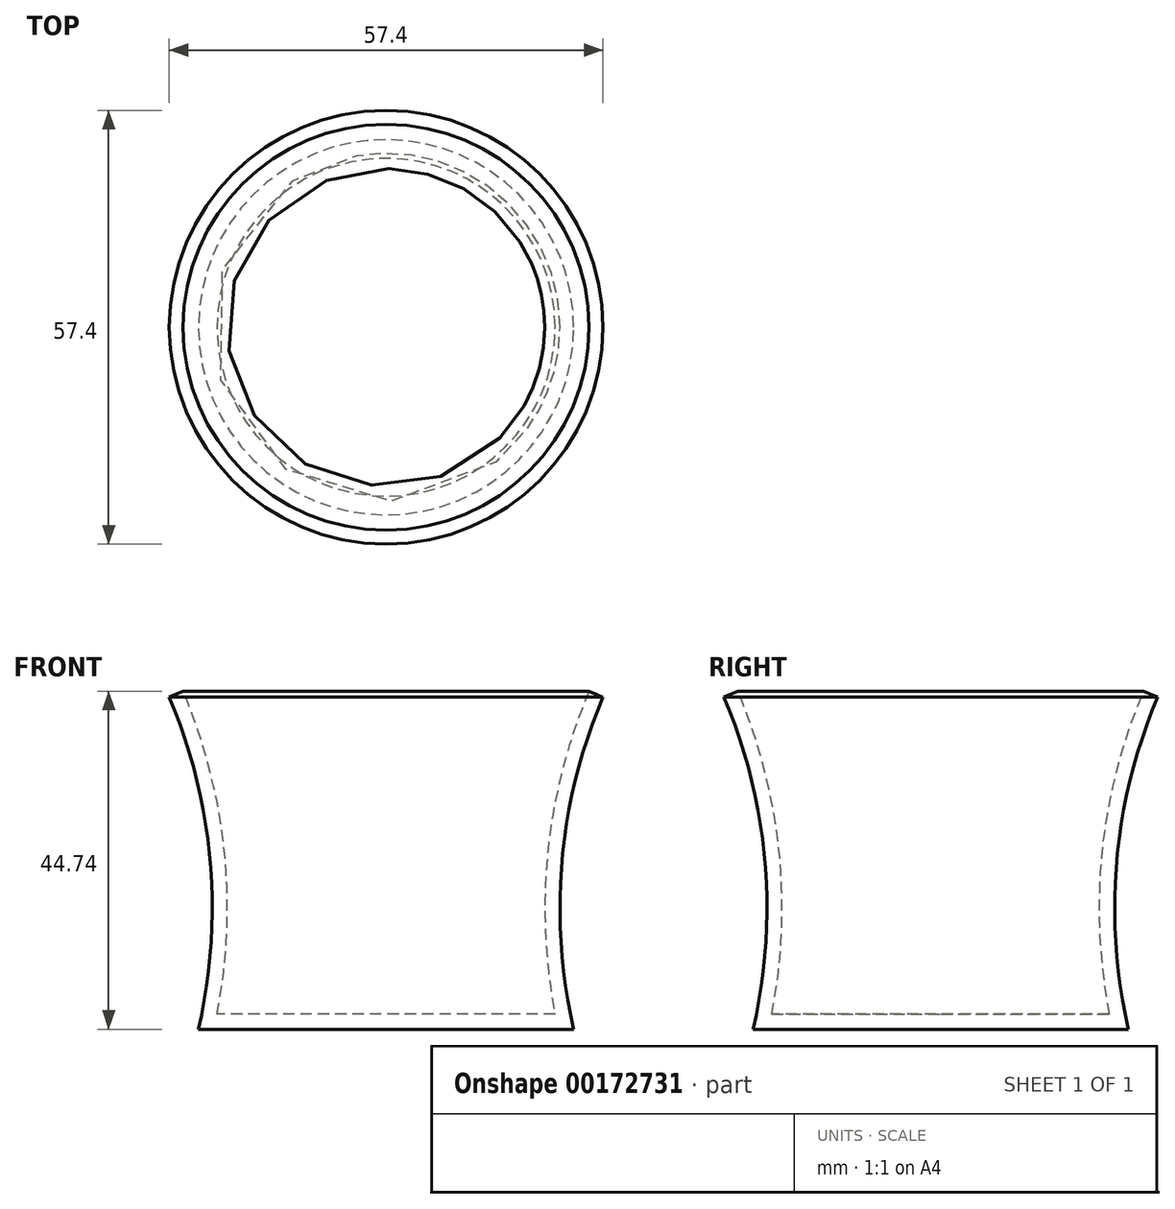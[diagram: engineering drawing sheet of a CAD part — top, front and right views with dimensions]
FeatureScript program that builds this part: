
annotation { "Feature Type Name" : "Feature", "Feature Type Description" : "" }
export const myFeature = defineFeature(function(context is Context, id is Id, definition is map)
    precondition{}
    {
        {
            var Q0;
            Q0=qCreatedBy(makeId("Front.planeOp"),FACE);
            var sketch = newSketch(context, id + "F0", { "sketchPlane" : qUnion([Q0])});
            skLineSegment(sketch, "E0", {"start": v(0, 0) * mm, "end": v(24.84, 0) * mm});
            skArc(sketch, "E1", {"start": v(28.7, 43.96) * mm, "mid": v(23.28, 22.29) * mm, "end": v(24.84, 0) * mm});
            skArc(sketch, "E2.0", {"start": v(26.86, 44.74) * mm, "mid": v(21.4, 23.7) * mm, "end": v(22.36, 2) * mm});
            skLineSegment(sketch, "E2.1", {"start": v(0, 2) * mm, "end": v(22.36, 2) * mm});
            skLineSegment(sketch, "E3", {"start": v(26.86, 44.74) * mm, "end": v(28.7, 43.96) * mm});
            skLineSegment(sketch, "E4", {"start": v(0, 2) * mm, "end": v(0, 0) * mm});
            skSolve(sketch);
        }
        {
            var Q0;
            Q0=makeQuery(id+"F0.imprint","IMPRINT",FACE,{"disambiguationData":[TD([[makeQuery(id+"F0.imprint","IMPRINT",EDGE,{"derivedFrom":sQuery(id+"F0.wireOp",EDGE,"E0")}),1.0]])]});
            var Q1;
            Q1=sQuery(id+"F0.wireOp",EDGE,"E4");
            revolve(context, id + "F1", {"entities" : qUnion([Q0]), "axis" : qUnion([Q1]), "revolveType" : RevolveType.FULL});
        }
    });
